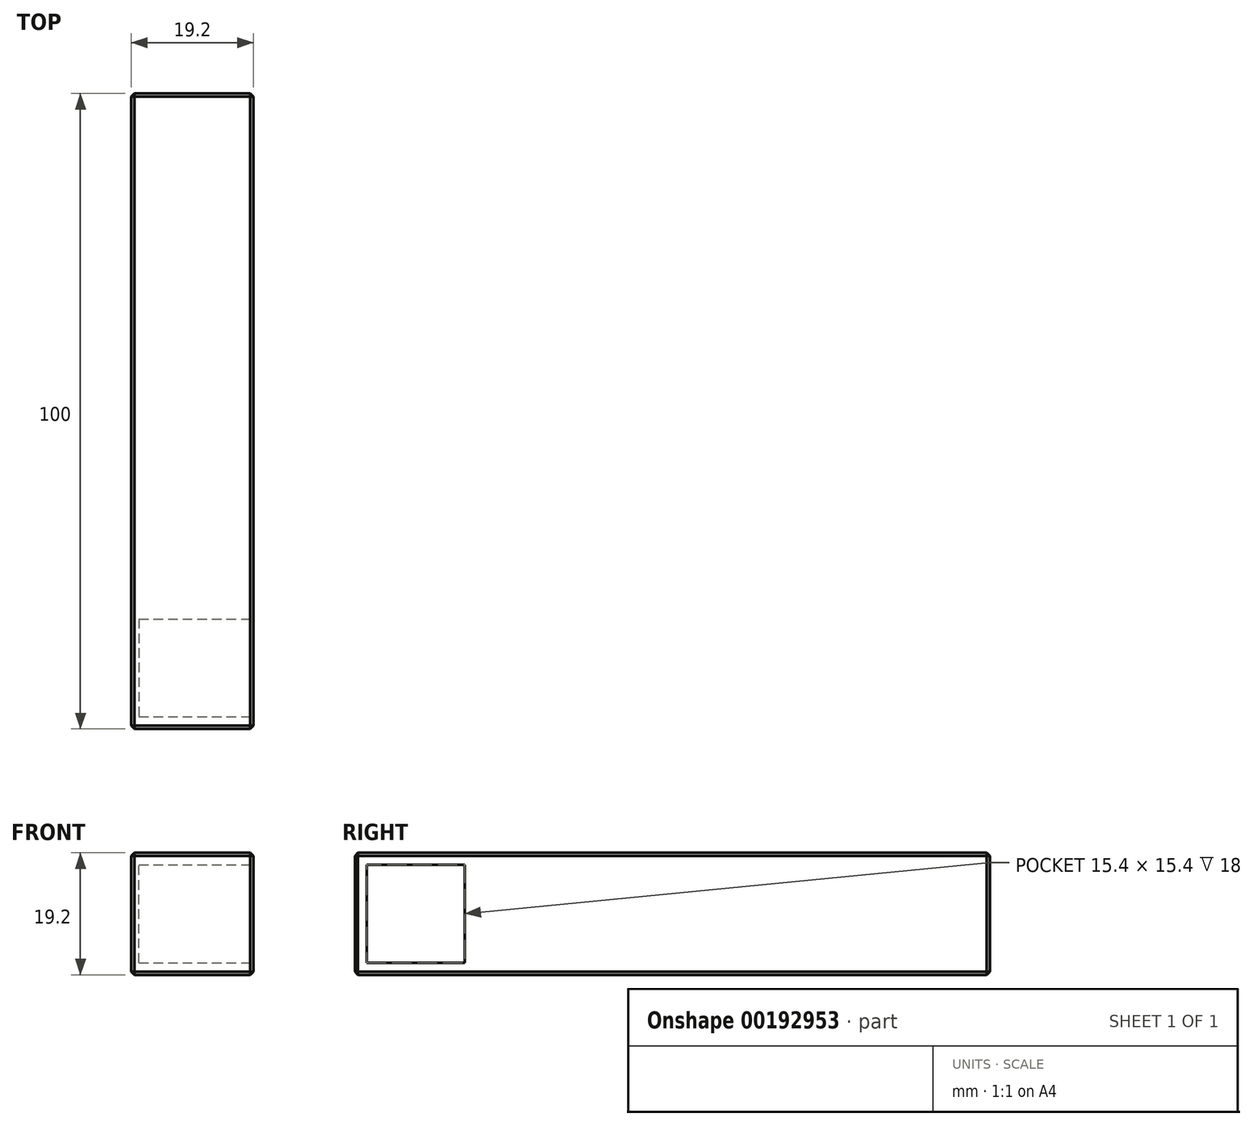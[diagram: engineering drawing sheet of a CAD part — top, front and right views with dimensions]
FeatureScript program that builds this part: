
annotation { "Feature Type Name" : "Feature", "Feature Type Description" : "" }
export const myFeature = defineFeature(function(context is Context, id is Id, definition is map)
    precondition{}
    {
        {
            var Q0;
            Q0=qCreatedBy(makeId("Top.planeOp"),FACE);
            var sketch = newSketch(context, id + "F0", { "sketchPlane" : qUnion([Q0])});
            skLineSegment(sketch, "E0.bottom", {"start": v(9.6, -50) * mm, "end": v(-9.6, -50) * mm});
            skLineSegment(sketch, "E0.top", {"start": v(9.6, 50) * mm, "end": v(-9.6, 50) * mm});
            skLineSegment(sketch, "E0.left", {"start": v(9.6, -50) * mm, "end": v(9.6, 50) * mm});
            skLineSegment(sketch, "E0.right", {"start": v(-9.6, -50) * mm, "end": v(-9.6, 50) * mm});
            skPoint(sketch, "E0.middle", {"position": v(0, 0) * mm});
            skSolve(sketch);
        }
        {
            var Q0;
            Q0 = qSketchRegion(id + "F0", true);
            extrude(context, id + "F1", {"entities" : qUnion([Q0]), "depth" : 19.2 * mm});
        }
        {
            var Q0;
            Q0=makeQuery(id+"F1.opExtrude","SWEPT_FACE",FACE,{"disambiguationData":[OSD([sQuery(id+"F0.wireOp",EDGE,"E0.left")])]});
            var sketch = newSketch(context, id + "F2", { "sketchPlane" : qUnion([Q0])});
            skLineSegment(sketch, "E1.bottom", {"start": v(-32.7, 1.9) * mm, "end": v(-48.1, 1.9) * mm});
            skLineSegment(sketch, "E1.top", {"start": v(-32.7, 17.3) * mm, "end": v(-48.1, 17.3) * mm});
            skLineSegment(sketch, "E1.left", {"start": v(-32.7, 1.9) * mm, "end": v(-32.7, 17.3) * mm});
            skLineSegment(sketch, "E1.right", {"start": v(-48.1, 1.9) * mm, "end": v(-48.1, 17.3) * mm});
            skPoint(sketch, "E1.middle", {"position": v(-40.4, 9.6) * mm});
            skPoint(sketch, "E1.middle.positionSnap0", {"position": v(-50, 9.6) * mm});
            skPoint(sketch, "E1.centerSnap0", {"position": v(-50, 9.6) * mm});
            skSolve(sketch);
        }
        {
            var Q0;
            Q0 = qSketchRegion(id + "F2", true);
            extrude(context, id + "F3", {"entities" : qUnion([Q0]), "operationType" : NewBodyOperationType.REMOVE, "oppositeDirection" : true, "depth" : 18 * mm});
        }
        {
            var Q0;
            Q0=makeQuery(id+"F1.opExtrude","SWEPT_FACE",FACE,{"disambiguationData":[OSD([sQuery(id+"F0.wireOp",EDGE,"E0.right")])]});
            var Q1;
            Q1=makeQuery(id+"F1.opExtrude","CAP_FACE",FACE,{"disambiguationData":[OSD([sQuery(id+"F0.wireOp",EDGE,"E0.bottom"),sQuery(id+"F0.wireOp",EDGE,"E0.top"),sQuery(id+"F0.wireOp",EDGE,"E0.left"),sQuery(id+"F0.wireOp",EDGE,"E0.right")])],"isStart":false});
            var Q2;
            Q2=makeQuery(id+"F1.opExtrude","SWEPT_FACE",FACE,{"disambiguationData":[OSD([sQuery(id+"F0.wireOp",EDGE,"E0.bottom")])]});
            var Q3;
            Q3=makeQuery(id+"F1.opExtrude","CAP_FACE",FACE,{"disambiguationData":[OSD([sQuery(id+"F0.wireOp",EDGE,"E0.bottom"),sQuery(id+"F0.wireOp",EDGE,"E0.top"),sQuery(id+"F0.wireOp",EDGE,"E0.left"),sQuery(id+"F0.wireOp",EDGE,"E0.right")])],"isStart":true});
            var Q4;
            Q4=makeQuery(id+"F1.opExtrude","SWEPT_FACE",FACE,{"disambiguationData":[OSD([sQuery(id+"F0.wireOp",EDGE,"E0.top")])]});
            chamfer(context, id + "F4", {"entities" : qUnion([Q0, Q1, Q2, Q3, Q4]), "width" : 0.5 * mm, "tangentPropagation" : true});
        }
    });
